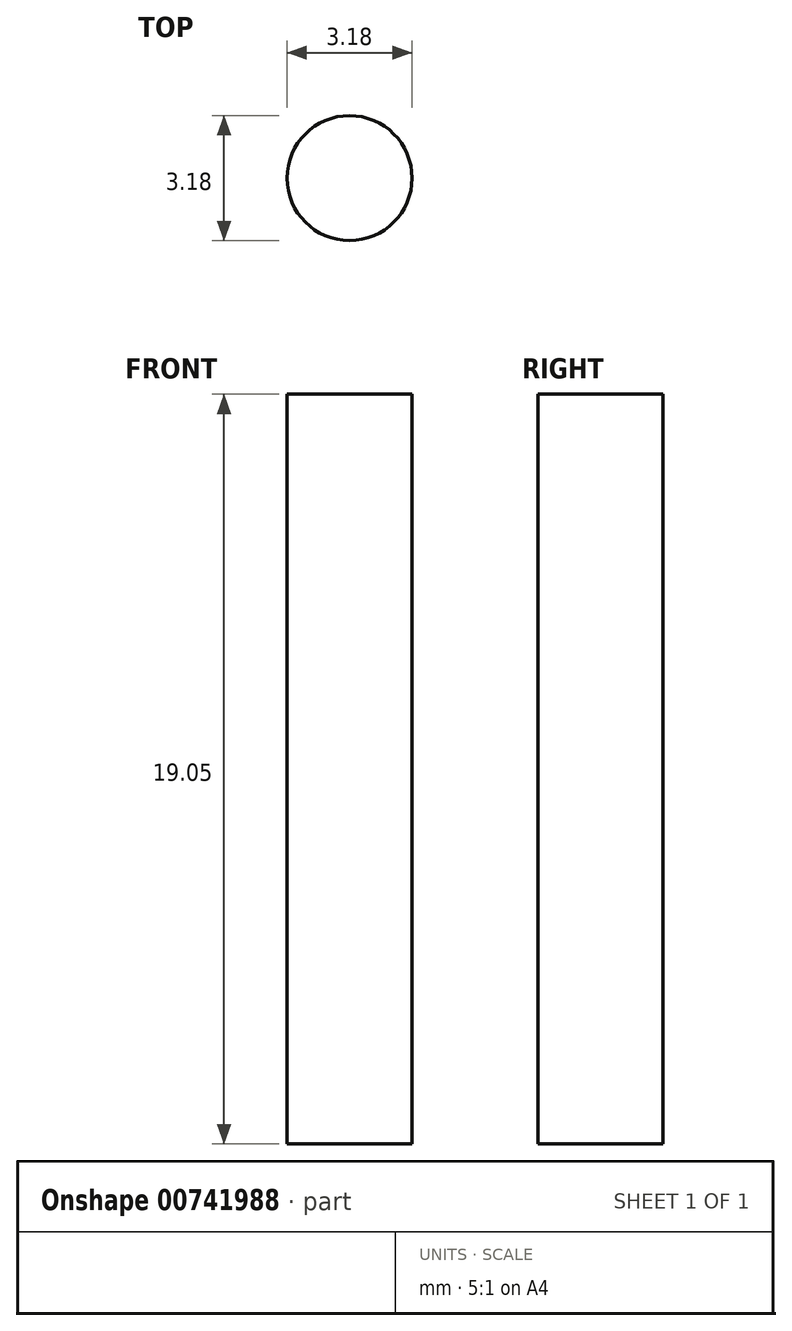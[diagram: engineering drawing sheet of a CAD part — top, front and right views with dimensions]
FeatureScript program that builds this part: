
annotation { "Feature Type Name" : "Feature", "Feature Type Description" : "" }
export const myFeature = defineFeature(function(context is Context, id is Id, definition is map)
    precondition{}
    {
        {
            var Q0;
            Q0=qCreatedBy(makeId("Top.planeOp"),FACE);
            var sketch = newSketch(context, id + "F0", { "sketchPlane" : qUnion([Q0])});
            skCircle(sketch, "E0", {"center": v(0, 0) * mm, "radius": 1.59 * mm});
            skSolve(sketch);
        }
        {
            var Q0;
            Q0 = qSketchRegion(id + "F0", true);
            extrude(context, id + "F1", {"entities" : qUnion([Q0]), "depth" : 19.05 * mm, "offsetDistance" : 25.4 * mm});
        }
    });
